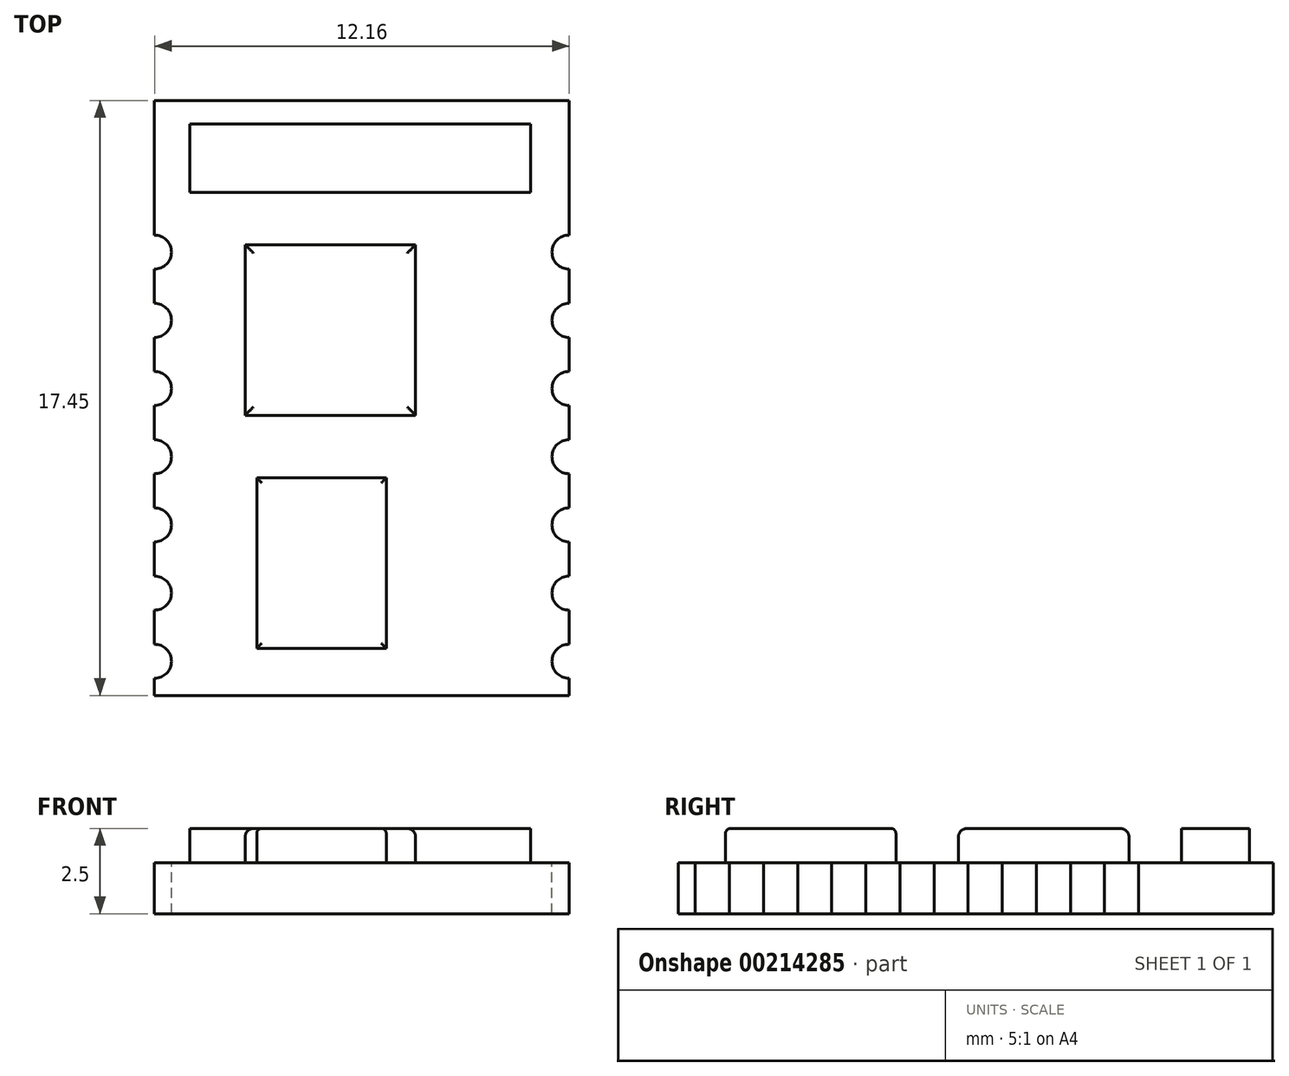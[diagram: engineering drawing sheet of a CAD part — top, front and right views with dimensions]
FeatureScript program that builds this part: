
annotation { "Feature Type Name" : "Feature", "Feature Type Description" : "" }
export const myFeature = defineFeature(function(context is Context, id is Id, definition is map)
    precondition{}
    {
        {
            var Q0;
            Q0=qCreatedBy(makeId("Top.planeOp"),FACE);
            var sketch = newSketch(context, id + "F0", { "sketchPlane" : qUnion([Q0])});
            skLineSegment(sketch, "E0.bottom", {"start": v(14.9, -15.88) * mm, "end": v(27.06, -15.88) * mm});
            skLineSegment(sketch, "E0.top", {"start": v(14.9, -33.33) * mm, "end": v(27.06, -33.33) * mm});
            skLineSegment(sketch, "E0.left", {"start": v(14.9, -15.88) * mm, "end": v(14.9, -33.33) * mm});
            skLineSegment(sketch, "E0.right", {"start": v(27.06, -15.88) * mm, "end": v(27.06, -33.33) * mm});
            skSolve(sketch);
        }
        {
            var Q0;
            Q0 = qSketchRegion(id + "F0", true);
            extrude(context, id + "F1", {"entities" : qUnion([Q0]), "depth" : 1.5 * mm});
        }
        {
            var Q0;
            Q0=makeQuery(id+"F1.opExtrude","CAP_FACE",FACE,{"disambiguationData":[OSD([sQuery(id+"F0.wireOp",EDGE,"E0.bottom"),sQuery(id+"F0.wireOp",EDGE,"E0.top"),sQuery(id+"F0.wireOp",EDGE,"E0.left"),sQuery(id+"F0.wireOp",EDGE,"E0.right")])],"isStart":false});
            var sketch = newSketch(context, id + "F2", { "sketchPlane" : qUnion([Q0])});
            skLineSegment(sketch, "E1.bottom", {"start": v(22.56, -25.11) * mm, "end": v(17.56, -25.11) * mm});
            skLineSegment(sketch, "E1.top", {"start": v(22.56, -20.11) * mm, "end": v(17.56, -20.11) * mm});
            skLineSegment(sketch, "E1.left", {"start": v(22.56, -25.11) * mm, "end": v(22.56, -20.11) * mm});
            skLineSegment(sketch, "E1.right", {"start": v(17.56, -25.11) * mm, "end": v(17.56, -20.11) * mm});
            skPoint(sketch, "E1.middle", {"position": v(20.06, -22.61) * mm});
            skLineSegment(sketch, "E2.bottom", {"start": v(17.9, -26.95) * mm, "end": v(21.7, -26.95) * mm});
            skLineSegment(sketch, "E2.top", {"start": v(17.9, -31.95) * mm, "end": v(21.7, -31.95) * mm});
            skLineSegment(sketch, "E2.left", {"start": v(17.9, -26.95) * mm, "end": v(17.9, -31.95) * mm});
            skLineSegment(sketch, "E2.right", {"start": v(21.7, -26.95) * mm, "end": v(21.7, -31.95) * mm});
            skLineSegment(sketch, "E3.bottom", {"start": v(15.93, -18.58) * mm, "end": v(25.93, -18.58) * mm});
            skLineSegment(sketch, "E3.top", {"start": v(15.93, -16.58) * mm, "end": v(25.93, -16.58) * mm});
            skLineSegment(sketch, "E3.left", {"start": v(15.93, -18.58) * mm, "end": v(15.93, -16.58) * mm});
            skLineSegment(sketch, "E3.right", {"start": v(25.93, -18.58) * mm, "end": v(25.93, -16.58) * mm});
            skPoint(sketch, "E3.middle", {"position": v(20.93, -17.58) * mm});
            skSolve(sketch);
        }
        {
            var Q0;
            Q0=makeQuery(id+"F1.opExtrude","CAP_FACE",FACE,{"disambiguationData":[OSD([sQuery(id+"F0.wireOp",EDGE,"E0.bottom"),sQuery(id+"F0.wireOp",EDGE,"E0.top"),sQuery(id+"F0.wireOp",EDGE,"E0.left"),sQuery(id+"F0.wireOp",EDGE,"E0.right")])],"isStart":false});
            var sketch = newSketch(context, id + "F3", { "sketchPlane" : qUnion([Q0])});
            skCircle(sketch, "E4", {"center": v(14.9, -32.33) * mm, "radius": 0.5 * mm});
            skCircle(sketch, "E5", {"center": v(27.06, -32.33) * mm, "radius": 0.5 * mm});
            skCircle(sketch, "E6.0.1.0", {"center": v(14.9, -30.33) * mm, "radius": 0.5 * mm});
            skCircle(sketch, "E6.0.1.1", {"center": v(27.06, -30.33) * mm, "radius": 0.5 * mm});
            skCircle(sketch, "E6.0.2.0", {"center": v(14.9, -28.33) * mm, "radius": 0.5 * mm});
            skCircle(sketch, "E6.0.2.1", {"center": v(27.06, -28.33) * mm, "radius": 0.5 * mm});
            skCircle(sketch, "E6.0.3.0", {"center": v(14.9, -26.33) * mm, "radius": 0.5 * mm});
            skCircle(sketch, "E6.0.3.1", {"center": v(27.06, -26.33) * mm, "radius": 0.5 * mm});
            skCircle(sketch, "E6.0.4.0", {"center": v(14.9, -24.33) * mm, "radius": 0.5 * mm});
            skCircle(sketch, "E6.0.4.1", {"center": v(27.06, -24.33) * mm, "radius": 0.5 * mm});
            skCircle(sketch, "E6.0.5.0", {"center": v(14.9, -22.33) * mm, "radius": 0.5 * mm});
            skCircle(sketch, "E6.0.5.1", {"center": v(27.06, -22.33) * mm, "radius": 0.5 * mm});
            skCircle(sketch, "E6.0.6.0", {"center": v(14.9, -20.33) * mm, "radius": 0.5 * mm});
            skCircle(sketch, "E6.0.6.1", {"center": v(27.06, -20.33) * mm, "radius": 0.5 * mm});
            skLineSegment(sketch, "E6.direction1", {"start": v(14.9, -32.33) * mm, "end": v(39.9, -32.33) * mm, "construction": true});
            skLineSegment(sketch, "E6.direction2", {"start": v(14.9, -32.33) * mm, "end": v(14.9, -30.33) * mm, "construction": true});
            skSolve(sketch);
        }
        {
            var Q0;
            Q0 = qSketchRegion(id + "F3", true);
            extrude(context, id + "F4", {"entities" : qUnion([Q0]), "operationType" : NewBodyOperationType.REMOVE, "endBound" : BoundingType.THROUGH_ALL, "oppositeDirection" : true, "depth" : 25 * mm});
        }
        {
            var Q0;
            Q0 = qSketchRegion(id + "F2", true);
            extrude(context, id + "F5", {"entities" : qUnion([Q0]), "depth" : 1 * mm});
        }
        {
            var Q0;
            Q0=makeQuery(id+"F5.opExtrude","CAP_EDGE",EDGE,{"disambiguationData":[OSD([sQuery(id+"F2.wireOp",EDGE,"E1.right")])],"isStart":false});
            var Q1;
            Q1=makeQuery(id+"F5.opExtrude","CAP_EDGE",EDGE,{"disambiguationData":[OSD([sQuery(id+"F2.wireOp",EDGE,"E1.bottom")])],"isStart":false});
            var Q2;
            Q2=makeQuery(id+"F5.opExtrude","CAP_EDGE",EDGE,{"disambiguationData":[OSD([sQuery(id+"F2.wireOp",EDGE,"E1.left")])],"isStart":false});
            var Q3;
            Q3=makeQuery(id+"F5.opExtrude","CAP_FACE",FACE,{"disambiguationData":[OSD([sQuery(id+"F2.wireOp",EDGE,"E1.bottom"),sQuery(id+"F2.wireOp",EDGE,"E1.top"),sQuery(id+"F2.wireOp",EDGE,"E1.left"),sQuery(id+"F2.wireOp",EDGE,"E1.right")])],"isStart":false});
            fillet(context, id + "F6", {"entities" : qUnion([Q0, Q1, Q2, Q3]), "radius" : 0.25 * mm, "tangentPropagation" : true, "allowEdgeOverflow" : false});
        }
        {
            var Q0;
            Q0=makeQuery(id+"F5.opExtrude","CAP_EDGE",EDGE,{"disambiguationData":[OSD([sQuery(id+"F2.wireOp",EDGE,"E2.left")])],"isStart":false});
            var Q1;
            Q1=makeQuery(id+"F5.opExtrude","CAP_EDGE",EDGE,{"disambiguationData":[OSD([sQuery(id+"F2.wireOp",EDGE,"E2.top")])],"isStart":false});
            var Q2;
            Q2=makeQuery(id+"F5.opExtrude","CAP_EDGE",EDGE,{"disambiguationData":[OSD([sQuery(id+"F2.wireOp",EDGE,"E2.right")])],"isStart":false});
            var Q3;
            Q3=makeQuery(id+"F5.opExtrude","CAP_EDGE",EDGE,{"disambiguationData":[OSD([sQuery(id+"F2.wireOp",EDGE,"E2.bottom")])],"isStart":false});
            fillet(context, id + "F7", {"entities" : qUnion([Q0, Q1, Q2, Q3]), "radius" : 0.15 * mm, "tangentPropagation" : true, "allowEdgeOverflow" : false});
        }
    });
